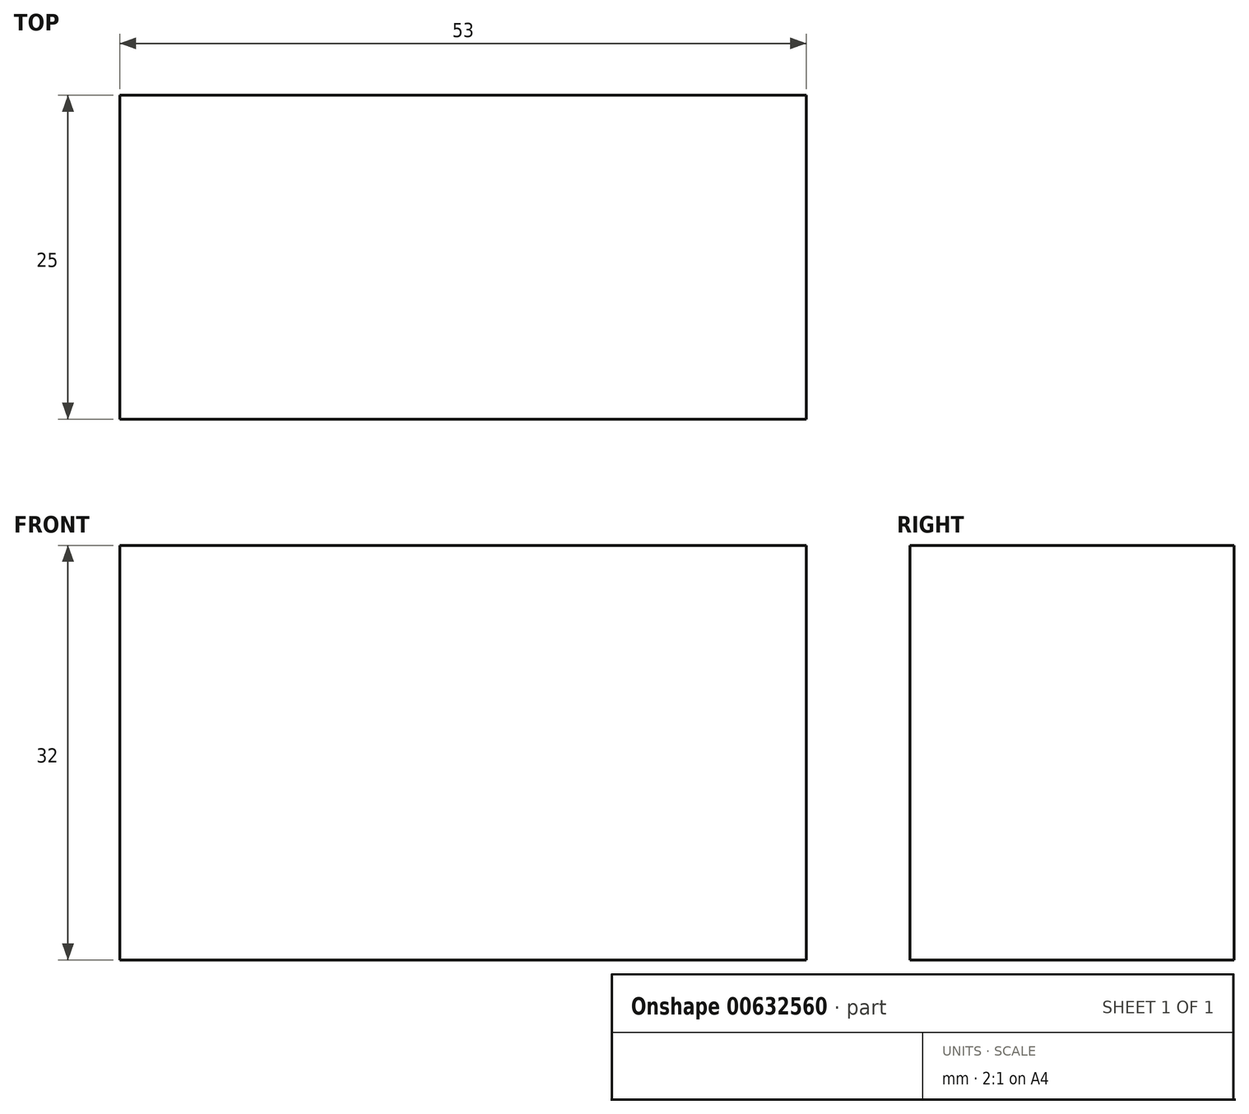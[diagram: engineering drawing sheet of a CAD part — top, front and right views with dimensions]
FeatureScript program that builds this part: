
annotation { "Feature Type Name" : "Feature", "Feature Type Description" : "" }
export const myFeature = defineFeature(function(context is Context, id is Id, definition is map)
    precondition{}
    {
        {
            var Q0;
            Q0=qCreatedBy(makeId("Front.planeOp"),FACE);
            var sketch = newSketch(context, id + "F0", { "sketchPlane" : qUnion([Q0])});
            skLineSegment(sketch, "E0.bottom", {"start": v(22.32, 10.16) * mm, "end": v(75.32, 10.16) * mm});
            skLineSegment(sketch, "E0.top", {"start": v(22.32, -21.84) * mm, "end": v(75.32, -21.84) * mm});
            skLineSegment(sketch, "E0.left", {"start": v(22.32, 10.16) * mm, "end": v(22.32, -21.84) * mm});
            skLineSegment(sketch, "E0.right", {"start": v(75.32, 10.16) * mm, "end": v(75.32, -21.84) * mm});
            skSolve(sketch);
        }
        {
            var Q0;
            Q0=makeQuery(id+"F0.imprint","IMPRINT",FACE,{"disambiguationData":[TD([[makeQuery(id+"F0.imprint","IMPRINT",EDGE,{"derivedFrom":sQuery(id+"F0.wireOp",EDGE,"E0.bottom")}),-1.0]])]});
            extrude(context, id + "F1", {"entities" : qUnion([Q0]), "depth" : 25 * mm, "offsetDistance" : 25.4 * mm});
        }
    });
